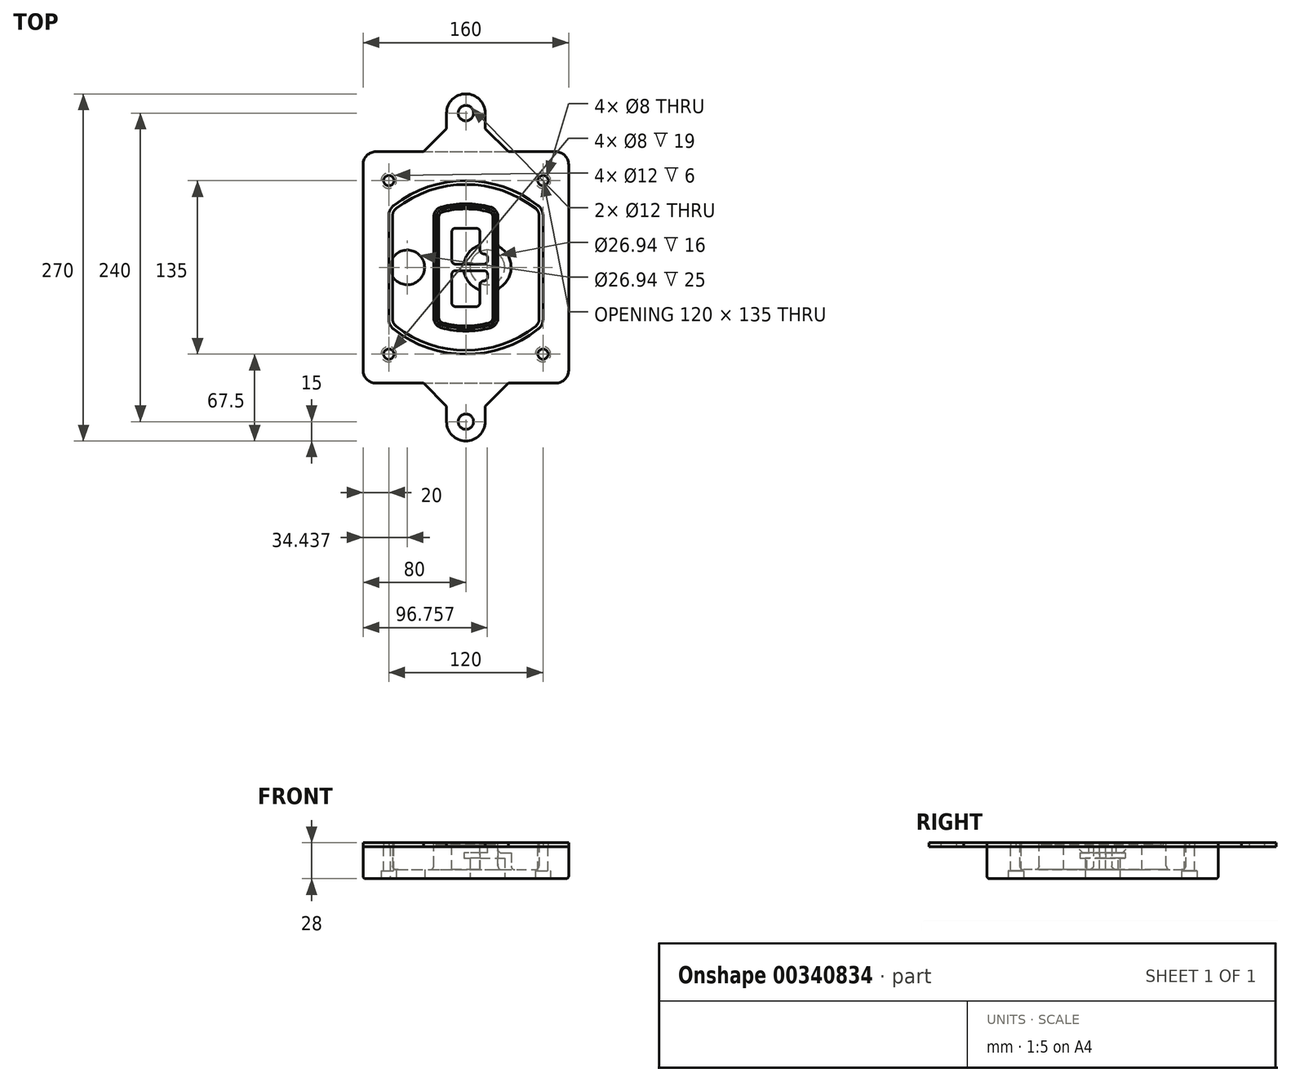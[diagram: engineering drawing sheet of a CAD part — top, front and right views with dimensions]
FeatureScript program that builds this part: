
annotation { "Feature Type Name" : "Feature", "Feature Type Description" : "" }
export const myFeature = defineFeature(function(context is Context, id is Id, definition is map)
    precondition{}
    {
        {
            var Q0;
            Q0=qCreatedBy(makeId("Top.planeOp"),FACE);
            var sketch = newSketch(context, id + "F0", { "sketchPlane" : qUnion([Q0])});
            skPoint(sketch, "E0.rect.middle", {"position": v(0, 0) * mm});
            skLineSegment(sketch, "E1.bottom", {"start": v(-70, -90) * mm, "end": v(70, -90) * mm});
            skLineSegment(sketch, "E1.top", {"start": v(-70, 90) * mm, "end": v(70, 90) * mm});
            skLineSegment(sketch, "E1.left", {"start": v(-80, -80) * mm, "end": v(-80, 80) * mm});
            skLineSegment(sketch, "E1.right", {"start": v(80, -80) * mm, "end": v(80, 80) * mm});
            skLineSegment(sketch, "E2", {"start": v(-80, 90) * mm, "end": v(80, -90) * mm, "construction": true});
            skLineSegment(sketch, "E3", {"start": v(80, 90) * mm, "end": v(-80, -90) * mm, "construction": true});
            skCircle(sketch, "E4", {"center": v(-60, 67.5) * mm, "radius": 4 * mm});
            skCircle(sketch, "E5", {"center": v(60, 67.5) * mm, "radius": 4 * mm});
            skCircle(sketch, "E6", {"center": v(60, -67.5) * mm, "radius": 4 * mm});
            skCircle(sketch, "E7", {"center": v(-60, -67.5) * mm, "radius": 4 * mm});
            skLineSegment(sketch, "E8", {"start": v(-60, 67.5) * mm, "end": v(60, 67.5) * mm, "construction": true});
            skLineSegment(sketch, "E9", {"start": v(60, 67.5) * mm, "end": v(60, -67.5) * mm, "construction": true});
            skLineSegment(sketch, "E10", {"start": v(60, -67.5) * mm, "end": v(-60, -67.5) * mm, "construction": true});
            skLineSegment(sketch, "E11", {"start": v(-60, -67.5) * mm, "end": v(-60, 67.5) * mm, "construction": true});
            skLineSegment(sketch, "E12", {"start": v(-60, 40.3) * mm, "end": v(-60, -40.3) * mm});
            skLineSegment(sketch, "E13", {"start": v(60, 40.3) * mm, "end": v(60, -40.3) * mm});
            skArc(sketch, "E14", {"start": v(56.15, 48.18) * mm, "mid": v(0, 67.5) * mm, "end": v(-56.15, 48.18) * mm});
            skArc(sketch, "E15", {"start": v(-56.15, -48.18) * mm, "mid": v(0, -67.5) * mm, "end": v(56.15, -48.18) * mm});
            skLineSegment(sketch, "E16", {"start": v(-60, 0) * mm, "end": v(60, 0) * mm, "construction": true});
            skPoint(sketch, "E17.visualSharp", {"position": v(-60, -45) * mm});
            skArc(sketch, "E17.filletArc", {"start": v(-60, -40.3) * mm, "mid": v(-58.99, -44.68) * mm, "end": v(-56.15, -48.18) * mm});
            skPoint(sketch, "E18.visualSharp", {"position": v(-60, 45) * mm});
            skArc(sketch, "E18.filletArc", {"start": v(-56.15, 48.18) * mm, "mid": v(-58.99, 44.68) * mm, "end": v(-60, 40.3) * mm});
            skPoint(sketch, "E19.visualSharp", {"position": v(60, 45) * mm});
            skArc(sketch, "E19.filletArc", {"start": v(60, 40.3) * mm, "mid": v(58.99, 44.68) * mm, "end": v(56.15, 48.18) * mm});
            skPoint(sketch, "E20.visualSharp", {"position": v(60, -45) * mm});
            skArc(sketch, "E20.filletArc", {"start": v(56.15, -48.18) * mm, "mid": v(58.99, -44.68) * mm, "end": v(60, -40.3) * mm});
            skPoint(sketch, "E21.visualSharp", {"position": v(-80, 90) * mm});
            skArc(sketch, "E21.filletArc", {"start": v(-70, 90) * mm, "mid": v(-77.07, 87.07) * mm, "end": v(-80, 80) * mm});
            skPoint(sketch, "E22.visualSharp", {"position": v(80, 90) * mm});
            skArc(sketch, "E22.filletArc", {"start": v(80, 80) * mm, "mid": v(77.07, 87.07) * mm, "end": v(70, 90) * mm});
            skPoint(sketch, "E23.visualSharp", {"position": v(80, -90) * mm});
            skArc(sketch, "E23.filletArc", {"start": v(70, -90) * mm, "mid": v(77.07, -87.07) * mm, "end": v(80, -80) * mm});
            skPoint(sketch, "E24.visualSharp", {"position": v(-80, -90) * mm});
            skArc(sketch, "E24.filletArc", {"start": v(-80, -80) * mm, "mid": v(-77.07, -87.07) * mm, "end": v(-70, -90) * mm});
            skArc(sketch, "E25.0", {"start": v(57, 40.3) * mm, "mid": v(56.3, 43.36) * mm, "end": v(54.3, 45.81) * mm});
            skLineSegment(sketch, "E25.1", {"start": v(57, 40.3) * mm, "end": v(57, -40.3) * mm});
            skArc(sketch, "E25.2", {"start": v(54.3, -45.81) * mm, "mid": v(56.3, -43.36) * mm, "end": v(57, -40.3) * mm});
            skArc(sketch, "E25.3", {"start": v(-54.3, -45.81) * mm, "mid": v(0, -64.5) * mm, "end": v(54.3, -45.81) * mm});
            skArc(sketch, "E25.4", {"start": v(-57, -40.3) * mm, "mid": v(-56.3, -43.36) * mm, "end": v(-54.3, -45.81) * mm});
            skArc(sketch, "E25.5", {"start": v(54.3, 45.81) * mm, "mid": v(0, 64.5) * mm, "end": v(-54.3, 45.81) * mm});
            skLineSegment(sketch, "E25.6", {"start": v(-57, 40.3) * mm, "end": v(-57, -40.3) * mm});
            skArc(sketch, "E25.7", {"start": v(-54.3, 45.81) * mm, "mid": v(-56.3, 43.36) * mm, "end": v(-57, 40.3) * mm});
            skArc(sketch, "E26.0", {"start": v(-58.62, 51.33) * mm, "mid": v(-62.58, 46.43) * mm, "end": v(-64, 40.3) * mm});
            skArc(sketch, "E26.1", {"start": v(58.62, 51.33) * mm, "mid": v(0, 71.5) * mm, "end": v(-58.62, 51.33) * mm});
            skArc(sketch, "E26.2", {"start": v(64, 40.3) * mm, "mid": v(62.58, 46.43) * mm, "end": v(58.62, 51.33) * mm});
            skLineSegment(sketch, "E26.3", {"start": v(64, 40.3) * mm, "end": v(64, -40.3) * mm});
            skArc(sketch, "E26.4", {"start": v(58.62, -51.33) * mm, "mid": v(62.58, -46.43) * mm, "end": v(64, -40.3) * mm});
            skLineSegment(sketch, "E26.5", {"start": v(-64, 40.3) * mm, "end": v(-64, -40.3) * mm});
            skArc(sketch, "E26.6", {"start": v(-58.62, -51.33) * mm, "mid": v(0, -71.5) * mm, "end": v(58.62, -51.33) * mm});
            skArc(sketch, "E26.7", {"start": v(-64, -40.3) * mm, "mid": v(-62.58, -46.43) * mm, "end": v(-58.62, -51.33) * mm});
            skSolve(sketch);
        }
        {
            var Q0;
            Q0=makeQuery(id+"F0.imprint","IMPRINT",FACE,{"disambiguationData":[TD([[makeQuery(id+"F0.imprint","IMPRINT",EDGE,{"derivedFrom":sQuery(id+"F0.wireOp",EDGE,"E1.bottom")}),1.0]])]});
            var Q1;
            Q1=makeQuery(id+"F0.imprint","IMPRINT",FACE,{"disambiguationData":[TD([[makeQuery(id+"F0.imprint","IMPRINT",EDGE,{"derivedFrom":sQuery(id+"F0.wireOp",EDGE,"E12")}),1.0]])]});
            var Q2;
            Q2=makeQuery(id+"F0.imprint","IMPRINT",FACE,{"disambiguationData":[TD([[makeQuery(id+"F0.imprint","IMPRINT",EDGE,{"derivedFrom":sQuery(id+"F0.wireOp",EDGE,"E25.0")}),1.0]])]});
            var Q3;
            Q3=makeQuery(id+"F0.imprint","IMPRINT",FACE,{"disambiguationData":[TD([[makeQuery(id+"F0.imprint","IMPRINT",EDGE,{"derivedFrom":sQuery(id+"F0.wireOp",EDGE,"E12")}),-1.0]])]});
            extrude(context, id + "F1", {"entities" : qUnion([Q0, Q1, Q2, Q3]), "oppositeDirection" : true, "depth" : 25 * mm});
        }
        {
            var Q0;
            Q0=makeQuery(id+"F0.imprint","IMPRINT",FACE,{"disambiguationData":[TD([[makeQuery(id+"F0.imprint","IMPRINT",EDGE,{"derivedFrom":sQuery(id+"F0.wireOp",EDGE,"E12")}),1.0]])]});
            extrude(context, id + "F2", {"entities" : qUnion([Q0]), "operationType" : NewBodyOperationType.ADD, "depth" : 3 * mm});
        }
        {
            var Q0;
            Q0=makeQuery(id+"F0.imprint","IMPRINT",FACE,{"disambiguationData":[TD([[makeQuery(id+"F0.imprint","IMPRINT",EDGE,{"derivedFrom":sQuery(id+"F0.wireOp",EDGE,"E25.0")}),1.0]])]});
            extrude(context, id + "F3", {"entities" : qUnion([Q0]), "operationType" : NewBodyOperationType.REMOVE, "oppositeDirection" : true, "depth" : 18 * mm});
        }
        {
            var Q0;
            Q0=makeQuery(id+"F2.opExtrude","CAP_FACE",FACE,{"disambiguationData":[OSD([sQuery(id+"F0.wireOp",EDGE,"E12"),sQuery(id+"F0.wireOp",EDGE,"E13"),sQuery(id+"F0.wireOp",EDGE,"E14"),sQuery(id+"F0.wireOp",EDGE,"E15"),sQuery(id+"F0.wireOp",EDGE,"E17.filletArc"),sQuery(id+"F0.wireOp",EDGE,"E18.filletArc"),sQuery(id+"F0.wireOp",EDGE,"E19.filletArc"),sQuery(id+"F0.wireOp",EDGE,"E20.filletArc"),sQuery(id+"F0.wireOp",EDGE,"E25.0"),sQuery(id+"F0.wireOp",EDGE,"E25.1"),sQuery(id+"F0.wireOp",EDGE,"E25.2"),sQuery(id+"F0.wireOp",EDGE,"E25.3"),sQuery(id+"F0.wireOp",EDGE,"E25.4"),sQuery(id+"F0.wireOp",EDGE,"E25.5"),sQuery(id+"F0.wireOp",EDGE,"E25.6"),sQuery(id+"F0.wireOp",EDGE,"E25.7")])],"isStart":false});
            var sketch = newSketch(context, id + "F4", { "sketchPlane" : qUnion([Q0])});
            skArc(sketch, "E27.0", {"start": v(-19.08, -46.97) * mm, "mid": v(0, -49.5) * mm, "end": v(19.08, -46.97) * mm});
            skArc(sketch, "E28.0", {"start": v(19.08, 46.97) * mm, "mid": v(0, 49.5) * mm, "end": v(-19.08, 46.97) * mm});
            skLineSegment(sketch, "E29", {"start": v(-25, 39.25) * mm, "end": v(-25, -39.25) * mm});
            skLineSegment(sketch, "E30", {"start": v(25, 39.25) * mm, "end": v(25, -39.25) * mm});
            skLineSegment(sketch, "E31", {"start": v(-25, 45.1) * mm, "end": v(25, 45.1) * mm, "construction": true});
            skLineSegment(sketch, "E32", {"start": v(-25, -45.1) * mm, "end": v(25, -45.1) * mm, "construction": true});
            skPoint(sketch, "E33.visualSharp", {"position": v(-25, 45.1) * mm});
            skArc(sketch, "E33.filletArc", {"start": v(-19.08, 46.97) * mm, "mid": v(-23.35, 44.11) * mm, "end": v(-25, 39.25) * mm});
            skPoint(sketch, "E34.visualSharp", {"position": v(25, 45.1) * mm});
            skArc(sketch, "E34.filletArc", {"start": v(25, 39.25) * mm, "mid": v(23.35, 44.11) * mm, "end": v(19.08, 46.97) * mm});
            skPoint(sketch, "E35.visualSharp", {"position": v(25, -45.1) * mm});
            skArc(sketch, "E35.filletArc", {"start": v(19.08, -46.97) * mm, "mid": v(23.35, -44.11) * mm, "end": v(25, -39.25) * mm});
            skPoint(sketch, "E36.visualSharp", {"position": v(-25, -45.1) * mm});
            skArc(sketch, "E36.filletArc", {"start": v(-25, -39.25) * mm, "mid": v(-23.35, -44.11) * mm, "end": v(-19.08, -46.97) * mm});
            skArc(sketch, "E37.0", {"start": v(54.3, 45.81) * mm, "mid": v(0, 64.5) * mm, "end": v(-54.3, 45.81) * mm});
            skArc(sketch, "E37.1", {"start": v(-54.3, 45.81) * mm, "mid": v(-56.3, 43.36) * mm, "end": v(-57, 40.3) * mm});
            skLineSegment(sketch, "E37.2", {"start": v(-57, 40.3) * mm, "end": v(-57, -40.3) * mm});
            skArc(sketch, "E37.3", {"start": v(-57, -40.3) * mm, "mid": v(-56.3, -43.36) * mm, "end": v(-54.3, -45.81) * mm});
            skArc(sketch, "E37.4", {"start": v(-54.3, -45.81) * mm, "mid": v(0, -64.5) * mm, "end": v(54.3, -45.81) * mm});
            skArc(sketch, "E37.5", {"start": v(54.3, -45.81) * mm, "mid": v(56.3, -43.36) * mm, "end": v(57, -40.3) * mm});
            skLineSegment(sketch, "E37.6", {"start": v(57, 40.3) * mm, "end": v(57, -40.3) * mm});
            skArc(sketch, "E37.7", {"start": v(57, 40.3) * mm, "mid": v(56.3, 43.36) * mm, "end": v(54.3, 45.81) * mm});
            skLineSegment(sketch, "E38.0", {"start": v(23, 39.25) * mm, "end": v(23, -39.25) * mm});
            skArc(sketch, "E38.1", {"start": v(18.56, -45.04) * mm, "mid": v(21.76, -42.9) * mm, "end": v(23, -39.25) * mm});
            skArc(sketch, "E38.2", {"start": v(-18.56, -45.04) * mm, "mid": v(0, -47.5) * mm, "end": v(18.56, -45.04) * mm});
            skArc(sketch, "E38.3", {"start": v(-23, -39.25) * mm, "mid": v(-21.76, -42.9) * mm, "end": v(-18.56, -45.04) * mm});
            skLineSegment(sketch, "E38.4", {"start": v(-23, 39.25) * mm, "end": v(-23, -39.25) * mm});
            skArc(sketch, "E38.5", {"start": v(23, 39.25) * mm, "mid": v(21.76, 42.9) * mm, "end": v(18.56, 45.04) * mm});
            skArc(sketch, "E38.6", {"start": v(-18.56, 45.04) * mm, "mid": v(-21.76, 42.9) * mm, "end": v(-23, 39.25) * mm});
            skArc(sketch, "E38.7", {"start": v(18.56, 45.04) * mm, "mid": v(0, 47.5) * mm, "end": v(-18.56, 45.04) * mm});
            skArc(sketch, "E39.0", {"start": v(21, 39.25) * mm, "mid": v(20.18, 41.68) * mm, "end": v(18.04, 43.1) * mm});
            skLineSegment(sketch, "E39.1", {"start": v(21, 39.25) * mm, "end": v(21, -39.25) * mm});
            skArc(sketch, "E39.2", {"start": v(18.04, -43.1) * mm, "mid": v(20.18, -41.68) * mm, "end": v(21, -39.25) * mm});
            skArc(sketch, "E39.3", {"start": v(-18.04, -43.1) * mm, "mid": v(0, -45.5) * mm, "end": v(18.04, -43.1) * mm});
            skArc(sketch, "E39.4", {"start": v(-21, -39.25) * mm, "mid": v(-20.18, -41.68) * mm, "end": v(-18.04, -43.1) * mm});
            skArc(sketch, "E39.5", {"start": v(18.04, 43.1) * mm, "mid": v(0, 45.5) * mm, "end": v(-18.04, 43.1) * mm});
            skLineSegment(sketch, "E39.6", {"start": v(-21, 39.25) * mm, "end": v(-21, -39.25) * mm});
            skArc(sketch, "E39.7", {"start": v(-18.04, 43.1) * mm, "mid": v(-20.18, 41.68) * mm, "end": v(-21, 39.25) * mm});
            skLineSegment(sketch, "E40", {"start": v(-25, 0) * mm, "end": v(25, 0) * mm, "construction": true});
            skLineSegment(sketch, "E41", {"start": v(-11, 5.5) * mm, "end": v(-11, 27.5) * mm});
            skLineSegment(sketch, "E42", {"start": v(-8, 30.5) * mm, "end": v(8, 30.5) * mm});
            skLineSegment(sketch, "E43", {"start": v(11, 27.5) * mm, "end": v(11, 13.5) * mm});
            skLineSegment(sketch, "E44", {"start": v(14, 10.5) * mm, "end": v(14, 10.5) * mm});
            skLineSegment(sketch, "E45", {"start": v(17, 7.5) * mm, "end": v(17, 5.5) * mm});
            skLineSegment(sketch, "E46", {"start": v(14, 2.5) * mm, "end": v(-8, 2.5) * mm});
            skPoint(sketch, "E47.visualSharp", {"position": v(-11, 30.5) * mm});
            skArc(sketch, "E47.filletArc", {"start": v(-8, 30.5) * mm, "mid": v(-10.12, 29.62) * mm, "end": v(-11, 27.5) * mm});
            skPoint(sketch, "E48.visualSharp", {"position": v(11, 30.5) * mm});
            skArc(sketch, "E48.filletArc", {"start": v(11, 27.5) * mm, "mid": v(10.12, 29.62) * mm, "end": v(8, 30.5) * mm});
            skPoint(sketch, "E49.visualSharp", {"position": v(11, 10.5) * mm});
            skArc(sketch, "E49.filletArc", {"start": v(11, 13.5) * mm, "mid": v(11.88, 11.38) * mm, "end": v(14, 10.5) * mm});
            skPoint(sketch, "E50.visualSharp", {"position": v(17, 10.5) * mm});
            skArc(sketch, "E50.filletArc", {"start": v(17, 7.5) * mm, "mid": v(16.12, 9.62) * mm, "end": v(14, 10.5) * mm});
            skPoint(sketch, "E51.visualSharp", {"position": v(17, 2.5) * mm});
            skArc(sketch, "E51.filletArc", {"start": v(14, 2.5) * mm, "mid": v(16.12, 3.38) * mm, "end": v(17, 5.5) * mm});
            skPoint(sketch, "E52.visualSharp", {"position": v(-11, 2.5) * mm});
            skArc(sketch, "E52.filletArc", {"start": v(-11, 5.5) * mm, "mid": v(-10.12, 3.38) * mm, "end": v(-8, 2.5) * mm});
            skLineSegment(sketch, "E53.0.MirrorCS", {"start": v(14, -2.5) * mm, "end": v(-8, -2.5) * mm});
            skArc(sketch, "E54.0.MirrorCS", {"start": v(-11, -5.5) * mm, "mid": v(-10.12, -3.38) * mm, "end": v(-8, -2.5) * mm});
            skLineSegment(sketch, "E55.0.MirrorCS", {"start": v(-11, -5.5) * mm, "end": v(-11, -27.5) * mm});
            skArc(sketch, "E56.0.MirrorCS", {"start": v(-8, -30.5) * mm, "mid": v(-10.12, -29.62) * mm, "end": v(-11, -27.5) * mm});
            skLineSegment(sketch, "E57.0.MirrorCS", {"start": v(-8, -30.5) * mm, "end": v(8, -30.5) * mm});
            skArc(sketch, "E58.0.MirrorCS", {"start": v(11, -27.5) * mm, "mid": v(10.12, -29.62) * mm, "end": v(8, -30.5) * mm});
            skLineSegment(sketch, "E59.0.MirrorCS", {"start": v(11, -27.5) * mm, "end": v(11, -13.5) * mm});
            skArc(sketch, "E60.0.MirrorCS", {"start": v(11, -13.5) * mm, "mid": v(11.88, -11.38) * mm, "end": v(14, -10.5) * mm});
            skArc(sketch, "E61.0.MirrorCS", {"start": v(17, -7.5) * mm, "mid": v(16.12, -9.62) * mm, "end": v(14, -10.5) * mm});
            skLineSegment(sketch, "E62.0.MirrorCS", {"start": v(17, -7.5) * mm, "end": v(17, -5.5) * mm});
            skArc(sketch, "E63.0.MirrorCS", {"start": v(14, -2.5) * mm, "mid": v(16.12, -3.38) * mm, "end": v(17, -5.5) * mm});
            skSolve(sketch);
        }
        {
            var Q0;
            Q0=makeQuery(id+"F4.imprint","IMPRINT",FACE,{"disambiguationData":[TD([[makeQuery(id+"F4.imprint","IMPRINT",EDGE,{"derivedFrom":sQuery(id+"F4.wireOp",EDGE,"E27.0")}),1.0]])]});
            var Q1;
            Q1=makeQuery(id+"F4.imprint","IMPRINT",FACE,{"disambiguationData":[TD([[makeQuery(id+"F4.imprint","IMPRINT",EDGE,{"derivedFrom":sQuery(id+"F4.wireOp",EDGE,"E38.0")}),-1.0]])]});
            var Q2;
            Q2=makeQuery(id+"F4.imprint","IMPRINT",FACE,{"disambiguationData":[TD([[makeQuery(id+"F4.imprint","IMPRINT",EDGE,{"derivedFrom":sQuery(id+"F4.wireOp",EDGE,"E39.0")}),1.0]])]});
            extrude(context, id + "F5", {"entities" : qUnion([Q0, Q1, Q2]), "operationType" : NewBodyOperationType.ADD, "endBound" : BoundingType.UP_TO_NEXT, "oppositeDirection" : true, "depth" : 25 * mm});
        }
        {
            var Q0;
            Q0=makeQuery(id+"F4.imprint","IMPRINT",FACE,{"disambiguationData":[TD([[makeQuery(id+"F4.imprint","IMPRINT",EDGE,{"derivedFrom":sQuery(id+"F4.wireOp",EDGE,"E38.0")}),-1.0]])]});
            extrude(context, id + "F6", {"entities" : qUnion([Q0]), "operationType" : NewBodyOperationType.REMOVE, "oppositeDirection" : true, "depth" : 2 * mm});
        }
        {
            var Q0;
            Q0=makeQuery(id+"F1.opExtrude","CAP_FACE",FACE,{"disambiguationData":[OSD([sQuery(id+"F0.wireOp",EDGE,"E1.bottom"),sQuery(id+"F0.wireOp",EDGE,"E1.top"),sQuery(id+"F0.wireOp",EDGE,"E1.left"),sQuery(id+"F0.wireOp",EDGE,"E1.right"),sQuery(id+"F0.wireOp",EDGE,"E4"),sQuery(id+"F0.wireOp",EDGE,"E5"),sQuery(id+"F0.wireOp",EDGE,"E6"),sQuery(id+"F0.wireOp",EDGE,"E7"),sQuery(id+"F0.wireOp",EDGE,"E21.filletArc"),sQuery(id+"F0.wireOp",EDGE,"E22.filletArc"),sQuery(id+"F0.wireOp",EDGE,"E23.filletArc"),sQuery(id+"F0.wireOp",EDGE,"E24.filletArc")])],"isStart":false});
            var sketch = newSketch(context, id + "F7", { "sketchPlane" : qUnion([Q0])});
            skCircle(sketch, "E64", {"center": v(16.76, 0) * mm, "radius": 13.47 * mm});
            skCircle(sketch, "E65", {"center": v(-45.56, 0) * mm, "radius": 13.47 * mm});
            skLineSegment(sketch, "E66", {"start": v(80, 0) * mm, "end": v(-80, 0) * mm});
            skCircle(sketch, "E67", {"center": v(16.76, 0) * mm, "radius": 18.47 * mm});
            skCircle(sketch, "E68", {"center": v(60, -67.5) * mm, "radius": 6 * mm});
            skCircle(sketch, "E69", {"center": v(-60, -67.5) * mm, "radius": 6 * mm});
            skCircle(sketch, "E70", {"center": v(-60, 67.5) * mm, "radius": 6 * mm});
            skCircle(sketch, "E71", {"center": v(60, 67.5) * mm, "radius": 6 * mm});
            skSolve(sketch);
        }
        {
            var Q0;
            {var subQ1=sQuery(id+"F7.wireOp",EDGE,"E66");var subQ4=sQuery(id+"F7.wireOp",EDGE,"E64");var subQ6=makeQuery(id+"F7.imprint","INTERSECT",VERTEX,{"disambiguationData":[OD(0.0)],"derivedFrom":[subQ4,subQ1]});Q0=makeQuery(id+"F7.imprint","IMPRINT",FACE,{"disambiguationData":[TD([[makeQuery(id+"F7.imprint","IMPRINT",EDGE,{"disambiguationData":[TD([[subQ6,-1.0]])],"derivedFrom":subQ4}),-1.0]])]});}
            var Q1;
            {var subQ0=sQuery(id+"F7.wireOp",EDGE,"E66");var subQ1=sQuery(id+"F7.wireOp",EDGE,"E64");var subQ3=makeQuery(id+"F7.imprint","INTERSECT",VERTEX,{"disambiguationData":[OD(0.0)],"derivedFrom":[subQ1,subQ0]});Q1=makeQuery(id+"F7.imprint","IMPRINT",FACE,{"disambiguationData":[TD([[makeQuery(id+"F7.imprint","IMPRINT",EDGE,{"disambiguationData":[TD([[subQ3,-1.0]])],"derivedFrom":subQ1}),1.0]])]});}
            var Q2;
            {var subQ0=sQuery(id+"F7.wireOp",EDGE,"E66");var subQ1=sQuery(id+"F7.wireOp",EDGE,"E64");var subQ3=makeQuery(id+"F7.imprint","INTERSECT",VERTEX,{"disambiguationData":[OD(0.0)],"derivedFrom":[subQ1,subQ0]});Q2=makeQuery(id+"F7.imprint","IMPRINT",FACE,{"disambiguationData":[TD([[makeQuery(id+"F7.imprint","IMPRINT",EDGE,{"disambiguationData":[TD([[subQ3,1.0]])],"derivedFrom":subQ1}),1.0]])]});}
            var Q3;
            {var subQ1=sQuery(id+"F7.wireOp",EDGE,"E66");var subQ4=sQuery(id+"F7.wireOp",EDGE,"E64");var subQ6=makeQuery(id+"F7.imprint","INTERSECT",VERTEX,{"disambiguationData":[OD(0.0)],"derivedFrom":[subQ4,subQ1]});Q3=makeQuery(id+"F7.imprint","IMPRINT",FACE,{"disambiguationData":[TD([[makeQuery(id+"F7.imprint","IMPRINT",EDGE,{"disambiguationData":[TD([[subQ6,1.0]])],"derivedFrom":subQ4}),-1.0]])]});}
            extrude(context, id + "F8", {"entities" : qUnion([Q0, Q1, Q2, Q3]), "operationType" : NewBodyOperationType.ADD, "oppositeDirection" : true, "depth" : 20 * mm});
        }
        {
            var Q0;
            {var subQ0=sQuery(id+"F7.wireOp",EDGE,"E66");var subQ1=sQuery(id+"F7.wireOp",EDGE,"E64");var subQ3=makeQuery(id+"F7.imprint","INTERSECT",VERTEX,{"disambiguationData":[OD(0.0)],"derivedFrom":[subQ1,subQ0]});Q0=makeQuery(id+"F7.imprint","IMPRINT",FACE,{"disambiguationData":[TD([[makeQuery(id+"F7.imprint","IMPRINT",EDGE,{"disambiguationData":[TD([[subQ3,-1.0]])],"derivedFrom":subQ1}),1.0]])]});}
            var Q1;
            {var subQ0=sQuery(id+"F7.wireOp",EDGE,"E66");var subQ1=sQuery(id+"F7.wireOp",EDGE,"E64");var subQ3=makeQuery(id+"F7.imprint","INTERSECT",VERTEX,{"disambiguationData":[OD(0.0)],"derivedFrom":[subQ1,subQ0]});Q1=makeQuery(id+"F7.imprint","IMPRINT",FACE,{"disambiguationData":[TD([[makeQuery(id+"F7.imprint","IMPRINT",EDGE,{"disambiguationData":[TD([[subQ3,1.0]])],"derivedFrom":subQ1}),1.0]])]});}
            extrude(context, id + "F9", {"entities" : qUnion([Q0, Q1]), "operationType" : NewBodyOperationType.REMOVE, "oppositeDirection" : true, "depth" : 16 * mm});
        }
        {
            var Q0;
            {var subQ0=sQuery(id+"F7.wireOp",EDGE,"E66");var subQ1=sQuery(id+"F7.wireOp",EDGE,"E65");var subQ3=makeQuery(id+"F7.imprint","INTERSECT",VERTEX,{"disambiguationData":[OD(0.0)],"derivedFrom":[subQ1,subQ0]});Q0=makeQuery(id+"F7.imprint","IMPRINT",FACE,{"disambiguationData":[TD([[makeQuery(id+"F7.imprint","IMPRINT",EDGE,{"disambiguationData":[TD([[subQ3,-1.0]])],"derivedFrom":subQ1}),1.0]])]});}
            var Q1;
            {var subQ0=sQuery(id+"F7.wireOp",EDGE,"E66");var subQ1=sQuery(id+"F7.wireOp",EDGE,"E65");var subQ3=makeQuery(id+"F7.imprint","INTERSECT",VERTEX,{"disambiguationData":[OD(0.0)],"derivedFrom":[subQ1,subQ0]});Q1=makeQuery(id+"F7.imprint","IMPRINT",FACE,{"disambiguationData":[TD([[makeQuery(id+"F7.imprint","IMPRINT",EDGE,{"disambiguationData":[TD([[subQ3,1.0]])],"derivedFrom":subQ1}),1.0]])]});}
            extrude(context, id + "F10", {"entities" : qUnion([Q0, Q1]), "operationType" : NewBodyOperationType.REMOVE, "oppositeDirection" : true, "depth" : 25 * mm});
        }
        {
            var Q0;
            Q0=makeQuery(id+"F7.imprint","IMPRINT",FACE,{"disambiguationData":[TD([[makeQuery(id+"F7.imprint","IMPRINT",EDGE,{"derivedFrom":sQuery(id+"F7.wireOp",EDGE,"E68")}),1.0]])]});
            var Q1;
            Q1=makeQuery(id+"F7.imprint","IMPRINT",FACE,{"disambiguationData":[TD([[makeQuery(id+"F7.imprint","IMPRINT",EDGE,{"derivedFrom":makeQuery(id+"F1.opExtrude","CAP_EDGE",EDGE,{"disambiguationData":[OSD([sQuery(id+"F0.wireOp",EDGE,"E5")])],"isStart":false})}),-1.0]])]});
            var Q2;
            Q2=makeQuery(id+"F7.imprint","IMPRINT",FACE,{"disambiguationData":[TD([[makeQuery(id+"F7.imprint","IMPRINT",EDGE,{"derivedFrom":sQuery(id+"F7.wireOp",EDGE,"E69")}),1.0]])]});
            var Q3;
            Q3=makeQuery(id+"F7.imprint","IMPRINT",FACE,{"disambiguationData":[TD([[makeQuery(id+"F7.imprint","IMPRINT",EDGE,{"derivedFrom":makeQuery(id+"F1.opExtrude","CAP_EDGE",EDGE,{"disambiguationData":[OSD([sQuery(id+"F0.wireOp",EDGE,"E4")])],"isStart":false})}),-1.0]])]});
            var Q4;
            Q4=makeQuery(id+"F7.imprint","IMPRINT",FACE,{"disambiguationData":[TD([[makeQuery(id+"F7.imprint","IMPRINT",EDGE,{"derivedFrom":sQuery(id+"F7.wireOp",EDGE,"E70")}),1.0]])]});
            var Q5;
            Q5=makeQuery(id+"F7.imprint","IMPRINT",FACE,{"disambiguationData":[TD([[makeQuery(id+"F7.imprint","IMPRINT",EDGE,{"derivedFrom":makeQuery(id+"F1.opExtrude","CAP_EDGE",EDGE,{"disambiguationData":[OSD([sQuery(id+"F0.wireOp",EDGE,"E7")])],"isStart":false})}),-1.0]])]});
            var Q6;
            Q6=makeQuery(id+"F7.imprint","IMPRINT",FACE,{"disambiguationData":[TD([[makeQuery(id+"F7.imprint","IMPRINT",EDGE,{"derivedFrom":sQuery(id+"F7.wireOp",EDGE,"E71")}),1.0]])]});
            var Q7;
            Q7=makeQuery(id+"F7.imprint","IMPRINT",FACE,{"disambiguationData":[TD([[makeQuery(id+"F7.imprint","IMPRINT",EDGE,{"derivedFrom":makeQuery(id+"F1.opExtrude","CAP_EDGE",EDGE,{"disambiguationData":[OSD([sQuery(id+"F0.wireOp",EDGE,"E6")])],"isStart":false})}),-1.0]])]});
            extrude(context, id + "F11", {"entities" : qUnion([Q0, Q1, Q2, Q3, Q4, Q5, Q6, Q7]), "operationType" : NewBodyOperationType.REMOVE, "oppositeDirection" : true, "depth" : 6 * mm});
        }
        {
            var Q0;
            Q0=makeQuery(id+"F9.boolean.opBoolean","COPY",FACE,{"derivedFrom":makeQuery(id+"F9.opExtrude","CAP_FACE",FACE,{"disambiguationData":[OSD([sQuery(id+"F7.wireOp",EDGE,"E64")])],"isStart":false})});
            var sketch = newSketch(context, id + "F12", { "sketchPlane" : qUnion([Q0])});
            skArc(sketch, "E72.0", {"start": v(11, 17.55) * mm, "mid": v(2.57, 11.82) * mm, "end": v(-1.54, 2.5) * mm});
            skArc(sketch, "E72.1", {"start": v(-1.54, -2.5) * mm, "mid": v(2.57, -11.82) * mm, "end": v(11, -17.55) * mm});
            skLineSegment(sketch, "E73", {"start": v(-1.54, -2.5) * mm, "end": v(14, -2.5) * mm});
            skLineSegment(sketch, "E74.0", {"start": v(14, 2.5) * mm, "end": v(-1.54, 2.5) * mm});
            skArc(sketch, "E74.1", {"start": v(14, 2.5) * mm, "mid": v(16.12, 3.38) * mm, "end": v(17, 5.5) * mm});
            skLineSegment(sketch, "E74.2", {"start": v(17, 7.5) * mm, "end": v(17, 5.5) * mm});
            skArc(sketch, "E74.3", {"start": v(17, 7.5) * mm, "mid": v(16.12, 9.62) * mm, "end": v(14, 10.5) * mm});
            skArc(sketch, "E74.4", {"start": v(11, 13.5) * mm, "mid": v(11.88, 11.38) * mm, "end": v(14, 10.5) * mm});
            skLineSegment(sketch, "E74.5", {"start": v(11, 17.55) * mm, "end": v(11, 13.5) * mm});
            skLineSegment(sketch, "E74.7", {"start": v(14, -2.5) * mm, "end": v(-1.54, -2.5) * mm});
            skArc(sketch, "E74.8", {"start": v(14, -2.5) * mm, "mid": v(16.12, -3.38) * mm, "end": v(17, -5.5) * mm});
            skLineSegment(sketch, "E74.9", {"start": v(17, -7.5) * mm, "end": v(17, -5.5) * mm});
            skArc(sketch, "E74.10", {"start": v(17, -7.5) * mm, "mid": v(16.12, -9.62) * mm, "end": v(14, -10.5) * mm});
            skArc(sketch, "E74.11", {"start": v(11, -13.5) * mm, "mid": v(11.88, -11.38) * mm, "end": v(14, -10.5) * mm});
            skLineSegment(sketch, "E74.12", {"start": v(11, -17.55) * mm, "end": v(11, -13.5) * mm});
            skPoint(sketch, "E75.orphan", {"position": v(11, -27.5) * mm});
            skPoint(sketch, "E76.orphan", {"position": v(-8, -2.5) * mm});
            skPoint(sketch, "E77.orphan", {"position": v(-8, 2.5) * mm});
            skPoint(sketch, "E78.orphan", {"position": v(11, 27.5) * mm});
            skSolve(sketch);
        }
        {
            var Q0;
            {var subQ7=sQuery(id+"F12.wireOp",EDGE,"E72.0");var subQ14=sQuery(id+"F12.wireOp",EDGE,"E72.1");var subQ16=sQuery(id+"F12.wireOp",EDGE,"E74.1");var subQ18=sQuery(id+"F12.wireOp",EDGE,"E74.8");Q0=qUnion([makeQuery(id+"F12.imprint","IMPRINT",FACE,{"disambiguationData":[TD([[makeQuery(id+"F12.imprint","IMPRINT",EDGE,{"derivedFrom":subQ7}),1.0]])]}),makeQuery(id+"F12.imprint","IMPRINT",FACE,{"disambiguationData":[TD([[makeQuery(id+"F12.imprint","IMPRINT",EDGE,{"derivedFrom":subQ14}),1.0]])]}),makeQuery(id+"F12.imprint","IMPRINT",FACE,{"disambiguationData":[TD([[makeQuery(id+"F12.imprint","IMPRINT",EDGE,{"derivedFrom":subQ16}),1.0]])]}),makeQuery(id+"F12.imprint","IMPRINT",FACE,{"disambiguationData":[TD([[makeQuery(id+"F12.imprint","IMPRINT",EDGE,{"derivedFrom":subQ18}),-1.0]])]})]);}
            var Q1;
            Q1=makeQuery(id+"F5.boolean.opBoolean","SPLIT",FACE,{"disambiguationData":[TD([makeQuery(id+"F5.opExtrude","SWEPT_FACE",FACE,{"disambiguationData":[OSD([sQuery(id+"F4.wireOp",EDGE,"E41")])]})])],"derivedFrom":makeQuery(id+"F3.boolean.opBoolean","COPY",FACE,{"derivedFrom":makeQuery(id+"F3.opExtrude","CAP_FACE",FACE,{"disambiguationData":[OSD([sQuery(id+"F0.wireOp",EDGE,"E25.0"),sQuery(id+"F0.wireOp",EDGE,"E25.1"),sQuery(id+"F0.wireOp",EDGE,"E25.2"),sQuery(id+"F0.wireOp",EDGE,"E25.3"),sQuery(id+"F0.wireOp",EDGE,"E25.4"),sQuery(id+"F0.wireOp",EDGE,"E25.5"),sQuery(id+"F0.wireOp",EDGE,"E25.6"),sQuery(id+"F0.wireOp",EDGE,"E25.7")])],"isStart":false})})});
            extrude(context, id + "F13", {"entities" : qUnion([Q0]), "operationType" : NewBodyOperationType.REMOVE, "endBound" : BoundingType.UP_TO_SURFACE, "endBoundEntityFace" : qUnion([Q1]), "depth" : 25 * mm});
        }
        {
            var Q0;
            Q0=makeQuery(id+"F3.boolean.opBoolean","COPY",EDGE,{"derivedFrom":makeQuery(id+"F3.opExtrude","CAP_EDGE",EDGE,{"disambiguationData":[OSD([sQuery(id+"F0.wireOp",EDGE,"E25.6")])],"isStart":false})});
            var Q1;
            Q1=makeQuery(id+"F8.boolean.opBoolean","INTERSECT",EDGE,{"derivedFrom":[makeQuery(id+"F5.opExtrude","SWEPT_FACE",FACE,{"disambiguationData":[OSD([sQuery(id+"F4.wireOp",EDGE,"E30")])]}),makeQuery(id+"F8.opExtrude","CAP_FACE",FACE,{"disambiguationData":[OSD([sQuery(id+"F7.wireOp",EDGE,"E67")])],"isStart":false})]});
            var Q2;
            Q2=makeQuery(id+"F8.boolean.opBoolean","INTERSECT",EDGE,{"disambiguationData":[OD(1.0)],"derivedFrom":[makeQuery(id+"F5.opExtrude","SWEPT_FACE",FACE,{"disambiguationData":[OSD([sQuery(id+"F4.wireOp",EDGE,"E30")])]}),makeQuery(id+"F8.opExtrude","SWEPT_FACE",FACE,{"disambiguationData":[OSD([sQuery(id+"F7.wireOp",EDGE,"E67")])]})]});
            var Q3;
            {var subQ0=sQuery(id+"F4.wireOp",EDGE,"E30");Q3=makeQuery(id+"F8.boolean.opBoolean","SPLIT",EDGE,{"disambiguationData":[TD([makeQuery(id+"F5.opExtrude","SWEPT_FACE",FACE,{"disambiguationData":[OSD([sQuery(id+"F4.wireOp",EDGE,"E35.filletArc")])]})])],"derivedFrom":makeQuery(id+"F5.opExtrude","CAP_EDGE",EDGE,{"disambiguationData":[OSD([subQ0])],"isStart":false})});}
            var Q4;
            {var subQ0=sQuery(id+"F0.wireOp",EDGE,"E25.7");var subQ1=sQuery(id+"F0.wireOp",EDGE,"E25.1");var subQ2=sQuery(id+"F0.wireOp",EDGE,"E25.6");var subQ3=sQuery(id+"F0.wireOp",EDGE,"E25.5");var subQ4=sQuery(id+"F0.wireOp",EDGE,"E25.4");var subQ5=sQuery(id+"F0.wireOp",EDGE,"E25.0");var subQ6=sQuery(id+"F0.wireOp",EDGE,"E25.2");var subQ7=sQuery(id+"F0.wireOp",EDGE,"E25.3");Q4=makeQuery(id+"F8.boolean.opBoolean","INTERSECT",EDGE,{"derivedFrom":[makeQuery(id+"F5.boolean.opBoolean","SPLIT",FACE,{"disambiguationData":[TD([makeQuery(id+"F2.opExtrude","SWEPT_FACE",FACE,{"disambiguationData":[OSD([subQ5])]})])],"derivedFrom":makeQuery(id+"F3.boolean.opBoolean","COPY",FACE,{"derivedFrom":makeQuery(id+"F3.opExtrude","CAP_FACE",FACE,{"disambiguationData":[OSD([subQ5,subQ1,subQ6,subQ7,subQ4,subQ3,subQ2,subQ0])],"isStart":false})})}),makeQuery(id+"F8.opExtrude","SWEPT_FACE",FACE,{"disambiguationData":[OSD([sQuery(id+"F7.wireOp",EDGE,"E67")])]})]});}
            var Q5;
            Q5=makeQuery(id+"F8.boolean.opBoolean","INTERSECT",EDGE,{"disambiguationData":[OD(0.0)],"derivedFrom":[makeQuery(id+"F5.opExtrude","SWEPT_FACE",FACE,{"disambiguationData":[OSD([sQuery(id+"F4.wireOp",EDGE,"E30")])]}),makeQuery(id+"F8.opExtrude","SWEPT_FACE",FACE,{"disambiguationData":[OSD([sQuery(id+"F7.wireOp",EDGE,"E67")])]})]});
            fillet(context, id + "F14", {"entities" : qUnion([Q0, Q1, Q2, Q3, Q4, Q5]), "radius" : 3 * mm, "tangentPropagation" : true, "allowEdgeOverflow" : false});
        }
        {
            var Q0;
            Q0=makeQuery(id+"F1.opExtrude","CAP_EDGE",EDGE,{"disambiguationData":[OSD([sQuery(id+"F0.wireOp",EDGE,"E1.bottom")])],"isStart":false});
            fillet(context, id + "F15", {"entities" : qUnion([Q0]), "radius" : 2 * mm, "tangentPropagation" : true, "allowEdgeOverflow" : false});
        }
        {
            var Q0;
            {var subQ0=sQuery(id+"F0.wireOp",EDGE,"E21.filletArc");var subQ1=sQuery(id+"F0.wireOp",EDGE,"E7");var subQ2=sQuery(id+"F0.wireOp",EDGE,"E6");var subQ3=sQuery(id+"F0.wireOp",EDGE,"E5");var subQ4=sQuery(id+"F0.wireOp",EDGE,"E4");var subQ5=sQuery(id+"F0.wireOp",EDGE,"E22.filletArc");var subQ6=sQuery(id+"F0.wireOp",EDGE,"E1.bottom");var subQ7=sQuery(id+"F0.wireOp",EDGE,"E1.right");var subQ8=sQuery(id+"F0.wireOp",EDGE,"E1.top");var subQ9=sQuery(id+"F0.wireOp",EDGE,"E1.left");var subQ10=sQuery(id+"F0.wireOp",EDGE,"E23.filletArc");var subQ11=sQuery(id+"F0.wireOp",EDGE,"E24.filletArc");Q0=makeQuery(id+"F2.boolean.opBoolean","SPLIT",FACE,{"disambiguationData":[TD([makeQuery(id+"F1.opExtrude","SWEPT_FACE",FACE,{"disambiguationData":[OSD([subQ6])]})])],"derivedFrom":makeQuery(id+"F1.opExtrude","CAP_FACE",FACE,{"disambiguationData":[OSD([subQ6,subQ8,subQ9,subQ7,subQ4,subQ3,subQ2,subQ1,subQ0,subQ5,subQ10,subQ11])],"isStart":true})});}
            var sketch = newSketch(context, id + "F16", { "sketchPlane" : qUnion([Q0])});
            skLineSegment(sketch, "E79.0", {"start": v(-70, 90) * mm, "end": v(70, 90) * mm});
            skArc(sketch, "E79.1", {"start": v(80, 80) * mm, "mid": v(77.07, 87.07) * mm, "end": v(70, 90) * mm});
            skLineSegment(sketch, "E79.2", {"start": v(80, -80) * mm, "end": v(80, 80) * mm});
            skCircle(sketch, "E79.3", {"center": v(60, 67.5) * mm, "radius": 4 * mm});
            skArc(sketch, "E79.4", {"start": v(56.15, 48.18) * mm, "mid": v(0, 67.5) * mm, "end": v(-56.15, 48.18) * mm});
            skArc(sketch, "E79.5", {"start": v(60, 40.3) * mm, "mid": v(58.99, 44.68) * mm, "end": v(56.15, 48.18) * mm});
            skLineSegment(sketch, "E79.6", {"start": v(60, 40.3) * mm, "end": v(60, -40.3) * mm});
            skArc(sketch, "E79.7", {"start": v(-56.15, 48.18) * mm, "mid": v(-58.99, 44.68) * mm, "end": v(-60, 40.3) * mm});
            skCircle(sketch, "E79.8", {"center": v(-60, 67.5) * mm, "radius": 4 * mm});
            skArc(sketch, "E79.9", {"start": v(-70, 90) * mm, "mid": v(-77.07, 87.07) * mm, "end": v(-80, 80) * mm});
            skLineSegment(sketch, "E79.10", {"start": v(-80, -80) * mm, "end": v(-80, 80) * mm});
            skLineSegment(sketch, "E79.11", {"start": v(-60, 40.3) * mm, "end": v(-60, -40.3) * mm});
            skArc(sketch, "E79.12", {"start": v(-60, -40.3) * mm, "mid": v(-58.99, -44.68) * mm, "end": v(-56.15, -48.18) * mm});
            skArc(sketch, "E79.13", {"start": v(-56.15, -48.18) * mm, "mid": v(0, -67.5) * mm, "end": v(56.15, -48.18) * mm});
            skArc(sketch, "E79.14", {"start": v(-80, -80) * mm, "mid": v(-77.07, -87.07) * mm, "end": v(-70, -90) * mm});
            skCircle(sketch, "E79.15", {"center": v(-60, -67.5) * mm, "radius": 4 * mm});
            skLineSegment(sketch, "E79.16", {"start": v(-70, -90) * mm, "end": v(70, -90) * mm});
            skCircle(sketch, "E79.17", {"center": v(60, -67.5) * mm, "radius": 4 * mm});
            skArc(sketch, "E79.18", {"start": v(56.15, -48.18) * mm, "mid": v(58.99, -44.68) * mm, "end": v(60, -40.3) * mm});
            skArc(sketch, "E79.19", {"start": v(70, -90) * mm, "mid": v(77.07, -87.07) * mm, "end": v(80, -80) * mm});
            skLineSegment(sketch, "E80", {"start": v(0, 90) * mm, "end": v(0, 120) * mm, "construction": true});
            skLineSegment(sketch, "E81", {"start": v(-33, 90) * mm, "end": v(-15, 108) * mm});
            skLineSegment(sketch, "E82", {"start": v(-15, 108) * mm, "end": v(-15, 120) * mm});
            skArc(sketch, "E83", {"start": v(15, 120) * mm, "mid": v(0, 135) * mm, "end": v(-15, 120) * mm});
            skLineSegment(sketch, "E84", {"start": v(15, 120) * mm, "end": v(15, 108) * mm});
            skLineSegment(sketch, "E85", {"start": v(15, 108) * mm, "end": v(33, 90) * mm});
            skCircle(sketch, "E86", {"center": v(0, 120) * mm, "radius": 6 * mm});
            skLineSegment(sketch, "E87", {"start": v(-80, 0) * mm, "end": v(80, 0) * mm, "construction": true});
            skLineSegment(sketch, "E88.MirrorCS", {"start": v(-33, -90) * mm, "end": v(-15, -108) * mm});
            skLineSegment(sketch, "E89.MirrorCS", {"start": v(-15, -108) * mm, "end": v(-15, -120) * mm});
            skArc(sketch, "E90.MirrorCS", {"start": v(15, -120) * mm, "mid": v(0, -135) * mm, "end": v(-15, -120) * mm});
            skLineSegment(sketch, "E91.MirrorCS", {"start": v(15, -120) * mm, "end": v(15, -108) * mm});
            skLineSegment(sketch, "E92.MirrorCS", {"start": v(15, -108) * mm, "end": v(33, -90) * mm});
            skCircle(sketch, "E93.MirrorC", {"center": v(0, -120) * mm, "radius": 6 * mm});
            skSolve(sketch);
        }
        {
            var Q0;
            Q0 = qSketchRegion(id + "F16", true);
            var Q1;
            Q1=makeQuery(id+"F2.opExtrude","CAP_FACE",FACE,{"disambiguationData":[OSD([sQuery(id+"F0.wireOp",EDGE,"E12"),sQuery(id+"F0.wireOp",EDGE,"E13"),sQuery(id+"F0.wireOp",EDGE,"E14"),sQuery(id+"F0.wireOp",EDGE,"E15"),sQuery(id+"F0.wireOp",EDGE,"E17.filletArc"),sQuery(id+"F0.wireOp",EDGE,"E18.filletArc"),sQuery(id+"F0.wireOp",EDGE,"E19.filletArc"),sQuery(id+"F0.wireOp",EDGE,"E20.filletArc"),sQuery(id+"F0.wireOp",EDGE,"E25.0"),sQuery(id+"F0.wireOp",EDGE,"E25.1"),sQuery(id+"F0.wireOp",EDGE,"E25.2"),sQuery(id+"F0.wireOp",EDGE,"E25.3"),sQuery(id+"F0.wireOp",EDGE,"E25.4"),sQuery(id+"F0.wireOp",EDGE,"E25.5"),sQuery(id+"F0.wireOp",EDGE,"E25.6"),sQuery(id+"F0.wireOp",EDGE,"E25.7")])],"isStart":false});
            extrude(context, id + "F17", {"entities" : qUnion([Q0]), "endBound" : BoundingType.UP_TO_SURFACE, "endBoundEntityFace" : qUnion([Q1]), "depth" : 10 * mm});
        }
    });
